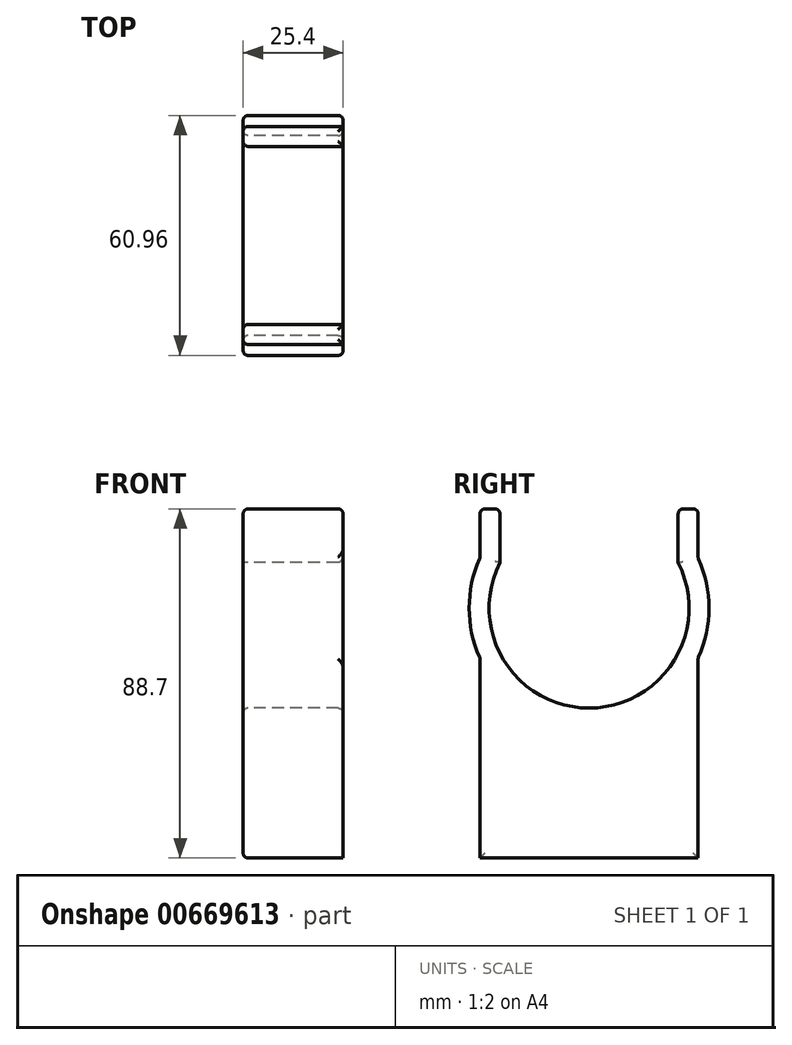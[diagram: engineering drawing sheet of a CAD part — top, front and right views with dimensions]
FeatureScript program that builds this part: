
annotation { "Feature Type Name" : "Feature", "Feature Type Description" : "" }
export const myFeature = defineFeature(function(context is Context, id is Id, definition is map)
    precondition{}
    {
        {
            var Q0;
            Q0=qCreatedBy(makeId("Right.planeOp"),FACE);
            var sketch = newSketch(context, id + "F0", { "sketchPlane" : qUnion([Q0])});
            skArc(sketch, "E0", {"start": v(-22.63, 11.54) * mm, "mid": v(-25.4, 0.26) * mm, "end": v(-22.86, -11.07) * mm});
            skLineSegment(sketch, "E1", {"start": v(-22.63, 11.54) * mm, "end": v(-22.63, 25.2) * mm});
            skLineSegment(sketch, "E2", {"start": v(22.63, 25.2) * mm, "end": v(22.63, 11.54) * mm});
            skArc(sketch, "E3", {"start": v(-27.7, 12.7) * mm, "mid": v(-30.48, 0) * mm, "end": v(-27.7, -12.7) * mm});
            skLineSegment(sketch, "E4.bottom", {"start": v(22.63, 25.2) * mm, "end": v(27.7, 25.2) * mm});
            skLineSegment(sketch, "E4.top", {"start": v(22.86, -63.5) * mm, "end": v(27.7, -63.5) * mm});
            skLineSegment(sketch, "E4.right", {"start": v(27.7, 25.2) * mm, "end": v(27.7, 12.7) * mm});
            skLineSegment(sketch, "E5.bottom", {"start": v(-22.63, 25.2) * mm, "end": v(-27.7, 25.2) * mm});
            skLineSegment(sketch, "E5.top", {"start": v(-22.86, -63.5) * mm, "end": v(-27.7, -63.5) * mm});
            skLineSegment(sketch, "E5.left", {"start": v(-22.63, 25.2) * mm, "end": v(-22.63, 11.54) * mm});
            skLineSegment(sketch, "E5.right", {"start": v(-27.7, 25.2) * mm, "end": v(-27.7, 12.7) * mm});
            skLineSegment(sketch, "E6.trimOffspring", {"start": v(-27.7, -12.7) * mm, "end": v(-27.7, -63.5) * mm});
            skArc(sketch, "E7.trimOffspring", {"start": v(27.7, -12.7) * mm, "mid": v(30.48, 0) * mm, "end": v(27.7, 12.7) * mm});
            skArc(sketch, "E8.trimOffspring", {"start": v(22.86, -11.07) * mm, "mid": v(25.4, 0.26) * mm, "end": v(22.63, 11.54) * mm});
            skLineSegment(sketch, "E9.trimOffspring", {"start": v(27.7, -12.7) * mm, "end": v(27.7, -63.5) * mm});
            skArc(sketch, "E10", {"start": v(-22.63, 11.54) * mm, "mid": v(0, -25.4) * mm, "end": v(22.63, 11.54) * mm});
            skLineSegment(sketch, "E11", {"start": v(-22.86, -63.5) * mm, "end": v(22.86, -63.5) * mm});
            skSolve(sketch);
        }
        {
            var Q0;
            Q0=makeQuery(id+"F0.imprint","IMPRINT",FACE,{"disambiguationData":[TD([[makeQuery(id+"F0.imprint","IMPRINT",EDGE,{"derivedFrom":sQuery(id+"F0.wireOp",EDGE,"E4.bottom")}),-1.0]])]});
            extrude(context, id + "F1", {"entities" : qUnion([Q0]), "endBound" : BoundingType.SYMMETRIC, "depth" : 25.4 * mm, "offsetDistance" : 25.4 * mm});
        }
        {
            var Q0;
            Q0=makeQuery(id+"F1.opExtrude","SWEPT_EDGE",EDGE,{"disambiguationData":[OSD([sQuery(id+"F0.wireOp",EDGE,"E5.bottom"),sQuery(id+"F0.wireOp",EDGE,"E5.left")])]});
            var Q1;
            Q1=makeQuery(id+"F1.opExtrude","SWEPT_EDGE",EDGE,{"disambiguationData":[OSD([sQuery(id+"F0.wireOp",EDGE,"E5.bottom"),sQuery(id+"F0.wireOp",EDGE,"E5.right")])]});
            var Q2;
            Q2=makeQuery(id+"F1.opExtrude","CAP_EDGE",EDGE,{"disambiguationData":[OSD([sQuery(id+"F0.wireOp",EDGE,"E5.bottom")])],"isStart":true});
            var Q3;
            Q3=makeQuery(id+"F1.opExtrude","CAP_EDGE",EDGE,{"disambiguationData":[OSD([sQuery(id+"F0.wireOp",EDGE,"E5.bottom")])],"isStart":false});
            var Q4;
            Q4=makeQuery(id+"F1.opExtrude","CAP_EDGE",EDGE,{"disambiguationData":[OSD([sQuery(id+"F0.wireOp",EDGE,"E4.bottom")])],"isStart":false});
            var Q5;
            Q5=makeQuery(id+"F1.opExtrude","CAP_EDGE",EDGE,{"disambiguationData":[OSD([sQuery(id+"F0.wireOp",EDGE,"E4.bottom")])],"isStart":true});
            var Q6;
            Q6=makeQuery(id+"F1.opExtrude","SWEPT_EDGE",EDGE,{"disambiguationData":[OSD([sQuery(id+"F0.wireOp",EDGE,"E4.bottom"),sQuery(id+"F0.wireOp",EDGE,"E2")])]});
            var Q7;
            Q7=makeQuery(id+"F1.opExtrude","SWEPT_EDGE",EDGE,{"disambiguationData":[OSD([sQuery(id+"F0.wireOp",EDGE,"E5.left"),sQuery(id+"F0.wireOp",EDGE,"E10")])]});
            var Q8;
            Q8=makeQuery(id+"F1.opExtrude","SWEPT_EDGE",EDGE,{"disambiguationData":[OSD([sQuery(id+"F0.wireOp",EDGE,"E2"),sQuery(id+"F0.wireOp",EDGE,"E10")])]});
            var Q9;
            Q9=makeQuery(id+"F1.opExtrude","SWEPT_EDGE",EDGE,{"disambiguationData":[OSD([sQuery(id+"F0.wireOp",EDGE,"E4.right"),sQuery(id+"F0.wireOp",EDGE,"E7.trimOffspring")])]});
            var Q10;
            Q10=makeQuery(id+"F1.opExtrude","SWEPT_EDGE",EDGE,{"disambiguationData":[OSD([sQuery(id+"F0.wireOp",EDGE,"E9.trimOffspring"),sQuery(id+"F0.wireOp",EDGE,"E7.trimOffspring")])]});
            var Q11;
            Q11=makeQuery(id+"F1.opExtrude","SWEPT_EDGE",EDGE,{"disambiguationData":[OSD([sQuery(id+"F0.wireOp",EDGE,"E5.right"),sQuery(id+"F0.wireOp",EDGE,"E3")])]});
            var Q12;
            Q12=makeQuery(id+"F1.opExtrude","SWEPT_EDGE",EDGE,{"disambiguationData":[OSD([sQuery(id+"F0.wireOp",EDGE,"E6.trimOffspring"),sQuery(id+"F0.wireOp",EDGE,"E3")])]});
            var Q13;
            Q13=makeQuery(id+"F1.opExtrude","CAP_EDGE",EDGE,{"disambiguationData":[OSD([sQuery(id+"F0.wireOp",EDGE,"E6.trimOffspring")])],"isStart":true});
            var Q14;
            Q14=makeQuery(id+"F1.opExtrude","CAP_FACE",FACE,{"disambiguationData":[OSD([sQuery(id+"F0.wireOp",EDGE,"E4.bottom"),sQuery(id+"F0.wireOp",EDGE,"E4.top"),sQuery(id+"F0.wireOp",EDGE,"E2"),sQuery(id+"F0.wireOp",EDGE,"E4.right"),sQuery(id+"F0.wireOp",EDGE,"E5.bottom"),sQuery(id+"F0.wireOp",EDGE,"E5.top"),sQuery(id+"F0.wireOp",EDGE,"E5.left"),sQuery(id+"F0.wireOp",EDGE,"E5.right"),sQuery(id+"F0.wireOp",EDGE,"E6.trimOffspring"),sQuery(id+"F0.wireOp",EDGE,"E9.trimOffspring"),sQuery(id+"F0.wireOp",EDGE,"E10"),sQuery(id+"F0.wireOp",EDGE,"E3"),sQuery(id+"F0.wireOp",EDGE,"E11"),sQuery(id+"F0.wireOp",EDGE,"E7.trimOffspring")])],"isStart":true});
            var Q15;
            Q15=makeQuery(id+"F1.opExtrude","CAP_EDGE",EDGE,{"disambiguationData":[OSD([sQuery(id+"F0.wireOp",EDGE,"E3")])],"isStart":false});
            var Q16;
            Q16=makeQuery(id+"F1.opExtrude","CAP_EDGE",EDGE,{"disambiguationData":[OSD([sQuery(id+"F0.wireOp",EDGE,"E10")])],"isStart":false});
            var Q17;
            Q17=makeQuery(id+"F1.opExtrude","CAP_EDGE",EDGE,{"disambiguationData":[OSD([sQuery(id+"F0.wireOp",EDGE,"E7.trimOffspring")])],"isStart":false});
            var Q18;
            Q18=makeQuery(id+"F1.opExtrude","CAP_EDGE",EDGE,{"disambiguationData":[OSD([sQuery(id+"F0.wireOp",EDGE,"E2")])],"isStart":false});
            fillet(context, id + "F2", {"entities" : qUnion([Q0, Q1, Q2, Q3, Q4, Q5, Q6, Q7, Q8, Q9, Q10, Q11, Q12, Q13, Q14, Q15, Q16, Q17, Q18]), "radius" : 1.27 * mm, "tangentPropagation" : true, "allowEdgeOverflow" : false});
        }
    });
